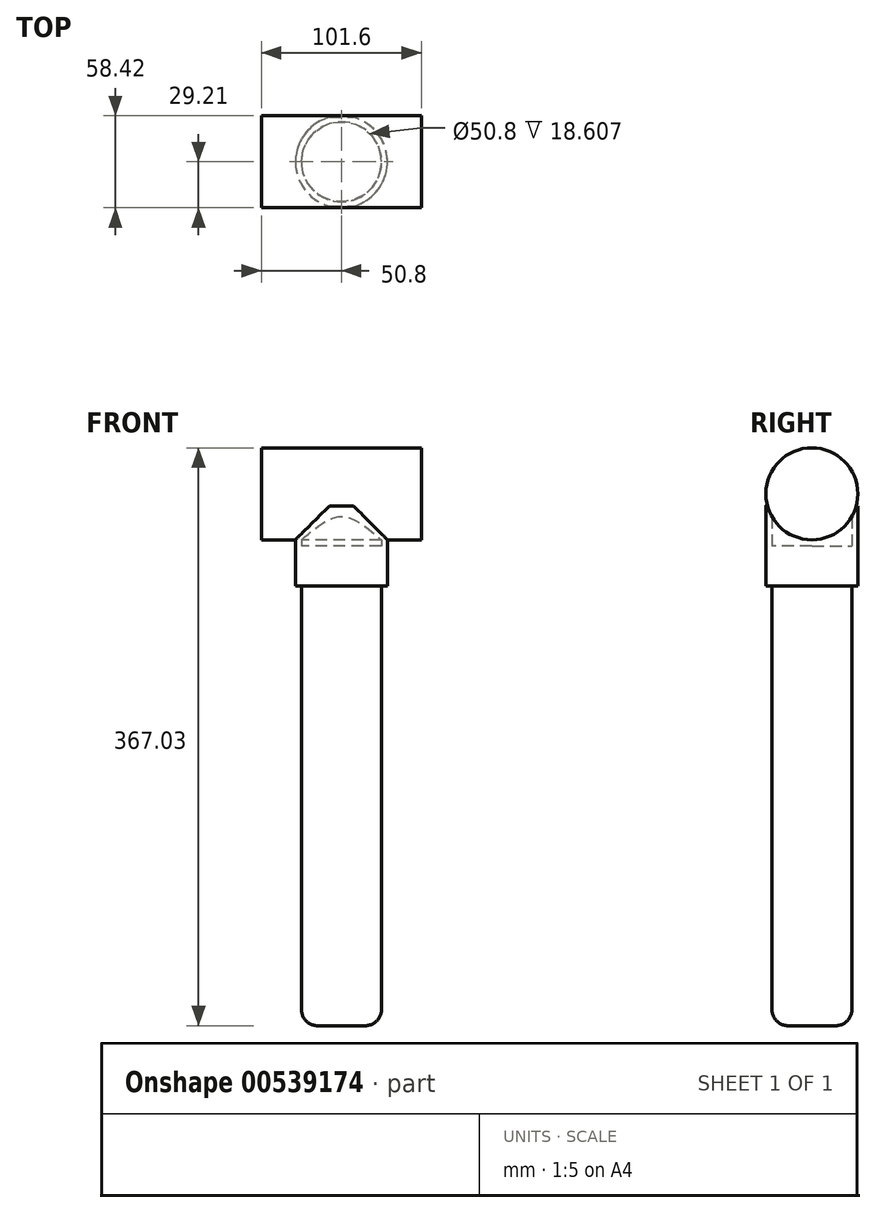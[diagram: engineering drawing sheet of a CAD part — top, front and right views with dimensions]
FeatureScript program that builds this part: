
annotation { "Feature Type Name" : "Feature", "Feature Type Description" : "" }
export const myFeature = defineFeature(function(context is Context, id is Id, definition is map)
    precondition{}
    {
        {
            var Q0;
            Q0=qCreatedBy(makeId("Front.planeOp"),FACE);
            var sketch = newSketch(context, id + "F0", { "sketchPlane" : qUnion([Q0])});
            skLineSegment(sketch, "E0.bottom", {"start": v(0, 0) * mm, "end": v(25.4, 0) * mm});
            skLineSegment(sketch, "E0.top", {"start": v(0, -304.8) * mm, "end": v(25.4, -304.8) * mm});
            skLineSegment(sketch, "E0.left", {"start": v(0, 0) * mm, "end": v(0, -304.8) * mm});
            skLineSegment(sketch, "E0.right", {"start": v(25.4, 0) * mm, "end": v(25.4, -304.8) * mm});
            skLineSegment(sketch, "E1", {"start": v(0, 0) * mm, "end": v(0, -75.99) * mm});
            skSolve(sketch);
        }
        {
            var Q0;
            Q0=makeQuery(id+"F0.imprint","IMPRINT",FACE,{"disambiguationData":[TD([[makeQuery(id+"F0.imprint","IMPRINT",EDGE,{"derivedFrom":sQuery(id+"F0.wireOp",EDGE,"E0.bottom")}),-1.0]])]});
            var Q1;
            Q1=sQuery(id+"F0.wireOp",EDGE,"E1");
            revolve(context, id + "F1", {"entities" : qUnion([Q0]), "axis" : qUnion([Q1]), "revolveType" : RevolveType.FULL});
        }
        {
            var Q0;
            Q0=qCreatedBy(makeId("Top.planeOp"),FACE);
            var sketch = newSketch(context, id + "F2", { "sketchPlane" : qUnion([Q0])});
            skCircle(sketch, "E2", {"center": v(0, 0) * mm, "radius": 29.21 * mm});
            skCircle(sketch, "E3", {"center": v(0, 0) * mm, "radius": 25.4 * mm});
            skSolve(sketch);
        }
        {
            var Q0;
            Q0 = qSketchRegion(id + "F2", true);
            extrude(context, id + "F3", {"entities" : qUnion([Q0]), "operationType" : NewBodyOperationType.ADD, "depth" : -25.4 * mm, "offsetDistance" : 25.4 * mm});
        }
        {
            var Q0;
            Q0 = qSketchRegion(id + "F2", true);
            extrude(context, id + "F4", {"entities" : qUnion([Q0]), "operationType" : NewBodyOperationType.ADD, "depth" : 25.4 * mm, "offsetDistance" : 25.4 * mm});
        }
        {
            var Q0;
            Q0=qCreatedBy(makeId("Right.planeOp"),FACE);
            var sketch = newSketch(context, id + "F5", { "sketchPlane" : qUnion([Q0])});
            skCircle(sketch, "E4", {"center": v(0, 33.02) * mm, "radius": 29.2 * mm});
            skSolve(sketch);
        }
        {
            var Q0;
            Q0 = qSketchRegion(id + "F5", true);
            extrude(context, id + "F6", {"entities" : qUnion([Q0]), "operationType" : NewBodyOperationType.REMOVE, "endBound" : BoundingType.SYMMETRIC, "oppositeDirection" : true, "depth" : 76.2 * mm, "offsetDistance" : 25.4 * mm});
        }
        {
            var Q0;
            Q0 = qSketchRegion(id + "F5", true);
            extrude(context, id + "F7", {"entities" : qUnion([Q0]), "operationType" : NewBodyOperationType.ADD, "endBound" : BoundingType.SYMMETRIC, "depth" : 101.6 * mm, "offsetDistance" : 25.4 * mm});
        }
        {
            var Q0;
            Q0=makeQuery(id+"F1.opRevolve","SWEPT_EDGE",EDGE,{"disambiguationData":[OSD([sQuery(id+"F0.wireOp",EDGE,"E0.top"),sQuery(id+"F0.wireOp",EDGE,"E0.right")])]});
            fillet(context, id + "F8", {"entities" : qUnion([Q0]), "radius" : 10.16 * mm, "tangentPropagation" : true, "allowEdgeOverflow" : false});
        }
    });
